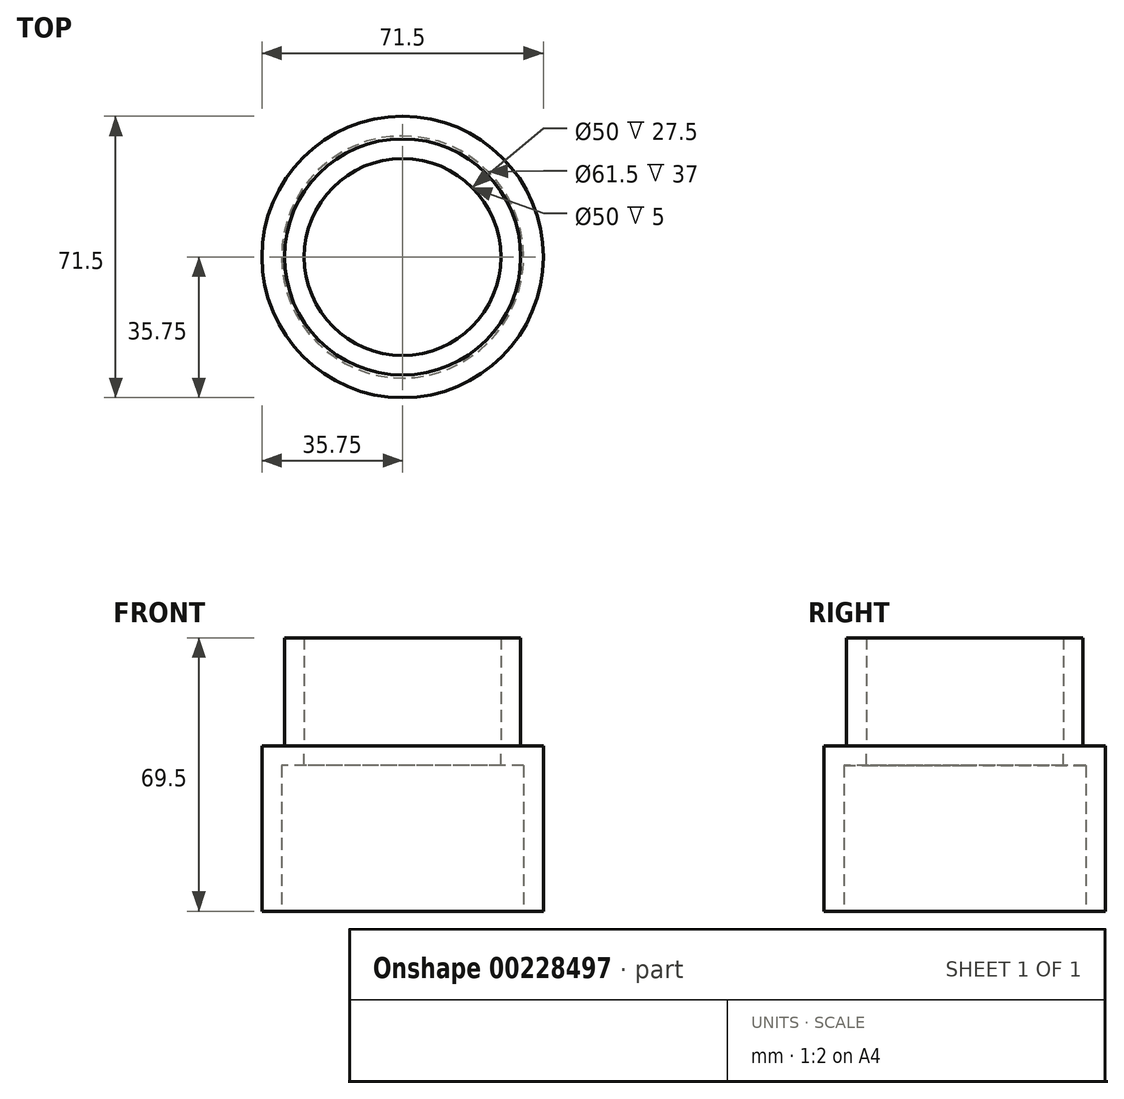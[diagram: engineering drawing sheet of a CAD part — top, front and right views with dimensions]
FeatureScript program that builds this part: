
annotation { "Feature Type Name" : "Feature", "Feature Type Description" : "" }
export const myFeature = defineFeature(function(context is Context, id is Id, definition is map)
    precondition{}
    {
        {
            var Q0;
            Q0=qCreatedBy(makeId("Top.planeOp"),FACE);
            var sketch = newSketch(context, id + "F0", { "sketchPlane" : qUnion([Q0])});
            skCircle(sketch, "E0", {"center": v(0, 0) * mm, "radius": 30.75 * mm});
            skSolve(sketch);
        }
        {
            var Q0;
            Q0=qCreatedBy(makeId("Top.planeOp"),FACE);
            var sketch = newSketch(context, id + "F1", { "sketchPlane" : qUnion([Q0])});
            skCircle(sketch, "E1.0", {"center": v(0, 0) * mm, "radius": 35.75 * mm});
            skSolve(sketch);
        }
        {
            var Q0;
            Q0=makeQuery(id+"F1.imprint","IMPRINT",FACE,{"disambiguationData":[TD([[makeQuery(id+"F1.imprint","IMPRINT",EDGE,{"derivedFrom":sQuery(id+"F1.wireOp",EDGE,"E1.0")}),1.0]])]});
            extrude(context, id + "F2", {"entities" : qUnion([Q0]), "depth" : 42 * mm});
        }
        {
            var Q0;
            Q0 = qSketchRegion(id + "F0", true);
            extrude(context, id + "F3", {"entities" : qUnion([Q0]), "operationType" : NewBodyOperationType.REMOVE, "depth" : 37 * mm});
        }
        {
            var Q0;
            Q0=makeQuery(id+"F2.opExtrude","CAP_FACE",FACE,{"disambiguationData":[OSD([sQuery(id+"F1.wireOp",EDGE,"E1.0")])],"isStart":false});
            var sketch = newSketch(context, id + "F4", { "sketchPlane" : qUnion([Q0])});
            skCircle(sketch, "E2", {"center": v(0, 0) * mm, "radius": 25 * mm});
            skSolve(sketch);
        }
        {
            var Q0;
            Q0=makeQuery(id+"F4.imprint","IMPRINT",FACE,{"disambiguationData":[TD([[makeQuery(id+"F4.imprint","IMPRINT",EDGE,{"derivedFrom":sQuery(id+"F4.wireOp",EDGE,"E2")}),-1.0]])]});
            var sketch = newSketch(context, id + "F5", { "sketchPlane" : qUnion([Q0])});
            skCircle(sketch, "E3.0", {"center": v(0, 0) * mm, "radius": 30 * mm});
            skSolve(sketch);
        }
        {
            var Q0;
            Q0=makeQuery(id+"F5.imprint","IMPRINT",FACE,{"disambiguationData":[TD([[makeQuery(id+"F5.imprint","IMPRINT",EDGE,{"derivedFrom":sQuery(id+"F5.wireOp",EDGE,"E3.0")}),1.0]])]});
            extrude(context, id + "F6", {"entities" : qUnion([Q0]), "depth" : 27.5 * mm});
        }
        {
            var Q0;
            Q0=makeQuery(id+"F4.imprint","IMPRINT",FACE,{"disambiguationData":[TD([[makeQuery(id+"F4.imprint","IMPRINT",EDGE,{"derivedFrom":sQuery(id+"F4.wireOp",EDGE,"E2")}),1.0]])]});
            extrude(context, id + "F7", {"entities" : qUnion([Q0]), "operationType" : NewBodyOperationType.REMOVE, "oppositeDirection" : true, "depth" : 25 * mm});
        }
    });
